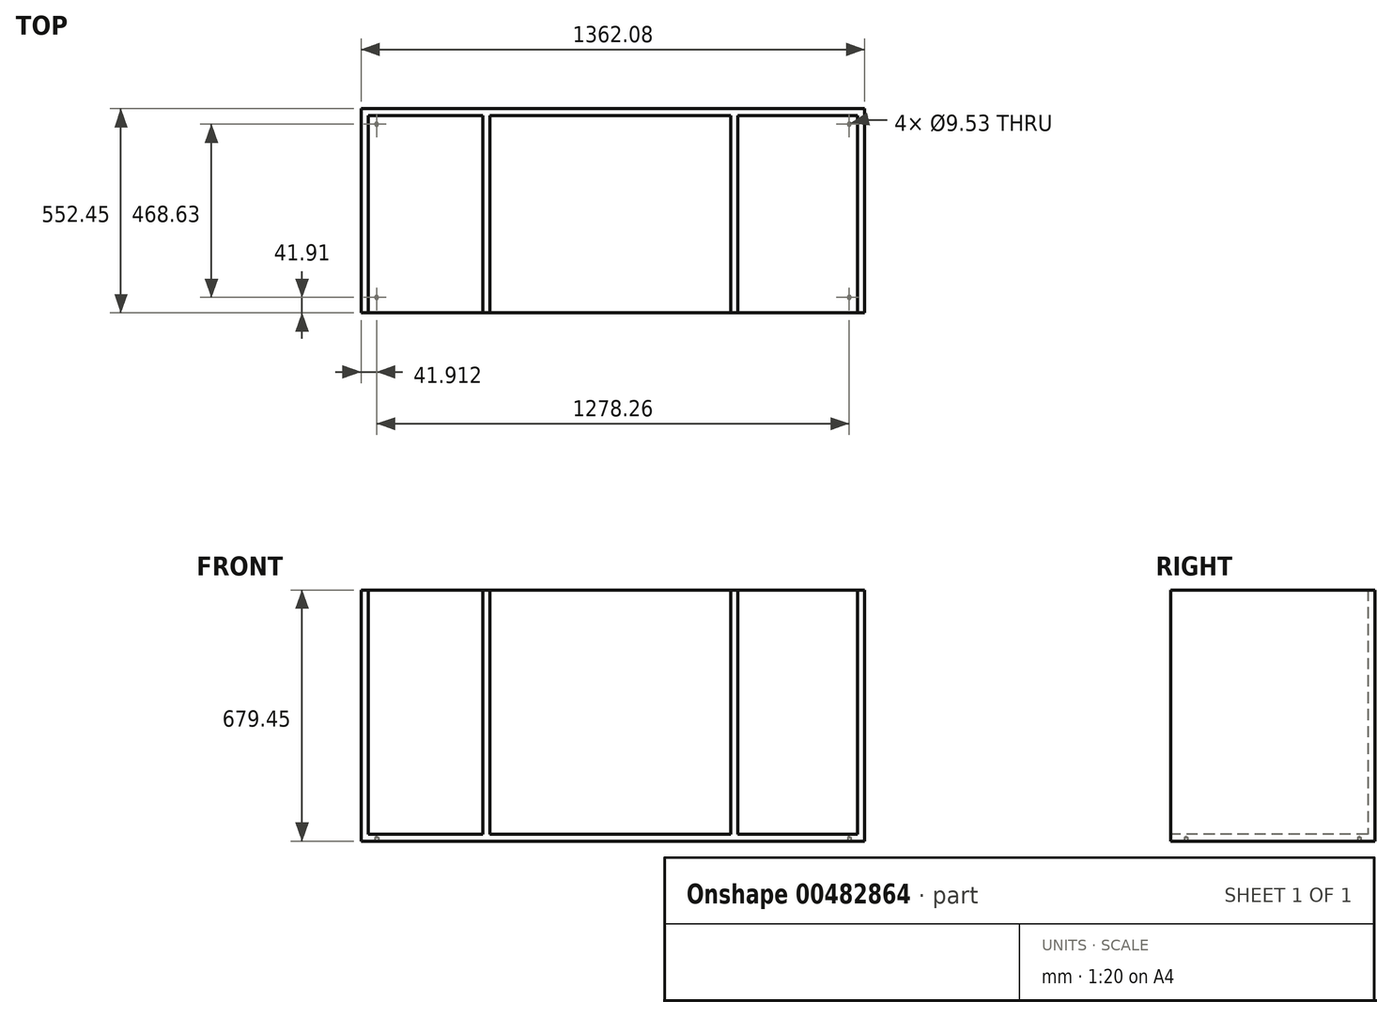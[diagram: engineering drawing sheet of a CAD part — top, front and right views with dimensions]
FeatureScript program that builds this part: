
annotation { "Feature Type Name" : "Feature", "Feature Type Description" : "" }
export const myFeature = defineFeature(function(context is Context, id is Id, definition is map)
    precondition{}
    {
        {
            var Q0;
            Q0=qCreatedBy(makeId("Front.planeOp"),FACE);
            var sketch = newSketch(context, id + "F0", { "sketchPlane" : qUnion([Q0])});
            skLineSegment(sketch, "E0", {"start": v(-681.04, 679.45) * mm, "end": v(-681.04, 0) * mm});
            skLineSegment(sketch, "E1", {"start": v(-681.04, 0) * mm, "end": v(681.04, 0) * mm});
            skLineSegment(sketch, "E2", {"start": v(681.04, 0) * mm, "end": v(681.04, 679.45) * mm});
            skLineSegment(sketch, "E3.0", {"start": v(661.99, 19.05) * mm, "end": v(661.99, 679.45) * mm});
            skLineSegment(sketch, "E3.1", {"start": v(-661.99, 19.05) * mm, "end": v(661.99, 19.05) * mm});
            skLineSegment(sketch, "E3.2", {"start": v(-661.99, 679.45) * mm, "end": v(-661.99, 19.05) * mm});
            skLineSegment(sketch, "E4", {"start": v(-681.04, 679.45) * mm, "end": v(-661.99, 679.45) * mm});
            skLineSegment(sketch, "E5", {"start": v(661.99, 679.45) * mm, "end": v(681.04, 679.45) * mm});
            skSolve(sketch);
        }
        {
            var Q0;
            Q0=makeQuery(id+"F0.imprint","IMPRINT",FACE,{"disambiguationData":[TD([[makeQuery(id+"F0.imprint","IMPRINT",EDGE,{"derivedFrom":sQuery(id+"F0.wireOp",EDGE,"E0")}),1.0]])]});
            extrude(context, id + "F1", {"entities" : qUnion([Q0]), "oppositeDirection" : true, "depth" : 533.4 * mm, "offsetDistance" : 25.4 * mm});
        }
        {
            var Q0;
            Q0=makeQuery(id+"F1.opExtrude","CAP_FACE",FACE,{"disambiguationData":[OSD([sQuery(id+"F0.wireOp",EDGE,"E0"),sQuery(id+"F0.wireOp",EDGE,"E1"),sQuery(id+"F0.wireOp",EDGE,"E2"),sQuery(id+"F0.wireOp",EDGE,"E3.0"),sQuery(id+"F0.wireOp",EDGE,"E3.1"),sQuery(id+"F0.wireOp",EDGE,"E3.2"),sQuery(id+"F0.wireOp",EDGE,"E4"),sQuery(id+"F0.wireOp",EDGE,"E5")])],"isStart":false});
            var sketch = newSketch(context, id + "F2", { "sketchPlane" : qUnion([Q0])});
            skLineSegment(sketch, "E6.0", {"start": v(-681.04, 0) * mm, "end": v(-681.04, 679.45) * mm});
            skLineSegment(sketch, "E7.0", {"start": v(681.04, 0) * mm, "end": v(-681.04, 0) * mm});
            skLineSegment(sketch, "E8.0", {"start": v(681.04, 679.45) * mm, "end": v(681.04, 0) * mm});
            skLineSegment(sketch, "E9", {"start": v(-681.04, 679.45) * mm, "end": v(681.04, 679.45) * mm});
            skSolve(sketch);
        }
        {
            var Q0;
            Q0 = qSketchRegion(id + "F2", true);
            extrude(context, id + "F3", {"entities" : qUnion([Q0]), "operationType" : NewBodyOperationType.ADD, "depth" : 19.05 * mm});
        }
        {
            var Q0;
            Q0=makeQuery(id+"F1.opExtrude","CAP_FACE",FACE,{"disambiguationData":[OSD([sQuery(id+"F0.wireOp",EDGE,"E0"),sQuery(id+"F0.wireOp",EDGE,"E1"),sQuery(id+"F0.wireOp",EDGE,"E2"),sQuery(id+"F0.wireOp",EDGE,"E3.0"),sQuery(id+"F0.wireOp",EDGE,"E3.1"),sQuery(id+"F0.wireOp",EDGE,"E3.2"),sQuery(id+"F0.wireOp",EDGE,"E4"),sQuery(id+"F0.wireOp",EDGE,"E5")])],"isStart":true});
            var sketch = newSketch(context, id + "F4", { "sketchPlane" : qUnion([Q0])});
            skLineSegment(sketch, "E10.bottom", {"start": v(-352.43, 679.45) * mm, "end": v(-333.38, 679.45) * mm});
            skLineSegment(sketch, "E10.top", {"start": v(-352.43, 19.05) * mm, "end": v(-333.38, 19.05) * mm});
            skLineSegment(sketch, "E10.left", {"start": v(-352.43, 679.45) * mm, "end": v(-352.43, 19.05) * mm});
            skLineSegment(sketch, "E10.right", {"start": v(-333.38, 679.45) * mm, "end": v(-333.38, 19.05) * mm});
            skLineSegment(sketch, "E11.bottom", {"start": v(319.09, 679.45) * mm, "end": v(338.14, 679.45) * mm});
            skLineSegment(sketch, "E11.top", {"start": v(319.09, 19.05) * mm, "end": v(338.14, 19.05) * mm});
            skLineSegment(sketch, "E11.left", {"start": v(319.09, 679.45) * mm, "end": v(319.09, 19.05) * mm});
            skLineSegment(sketch, "E11.right", {"start": v(338.14, 679.45) * mm, "end": v(338.14, 19.05) * mm});
            skSolve(sketch);
        }
        {
            var Q0;
            Q0 = qSketchRegion(id + "F4", true);
            var Q1;
            Q1=makeQuery(id+"F3.opExtrude","CAP_FACE",FACE,{"disambiguationData":[OSD([sQuery(id+"F2.wireOp",EDGE,"E6.0"),sQuery(id+"F2.wireOp",EDGE,"E7.0"),sQuery(id+"F2.wireOp",EDGE,"E8.0"),sQuery(id+"F2.wireOp",EDGE,"E9")])],"isStart":true});
            extrude(context, id + "F5", {"entities" : qUnion([Q0]), "operationType" : NewBodyOperationType.ADD, "endBound" : BoundingType.UP_TO_SURFACE, "oppositeDirection" : true, "endBoundEntityFace" : qUnion([Q1]), "depth" : 25.4 * mm});
        }
        {
            var Q0;
            Q0=makeQuery(id+"F3.boolean.opBoolean","MERGE",FACE,{"derivedFrom":[makeQuery(id+"F1.opExtrude","SWEPT_FACE",FACE,{"disambiguationData":[OSD([sQuery(id+"F0.wireOp",EDGE,"E1")])]}),makeQuery(id+"F3.opExtrude","SWEPT_FACE",FACE,{"disambiguationData":[OSD([sQuery(id+"F2.wireOp",EDGE,"E7.0")])]})]});
            var sketch = newSketch(context, id + "F6", { "sketchPlane" : qUnion([Q0])});
            skPoint(sketch, "E12", {"position": v(-639.13, -41.91) * mm});
            skPoint(sketch, "E13", {"position": v(-639.13, -510.54) * mm});
            skPoint(sketch, "E14", {"position": v(639.13, -510.54) * mm});
            skPoint(sketch, "E15", {"position": v(639.13, -41.91) * mm});
            skLineSegment(sketch, "E16.bottom", {"start": v(-639.13, -41.91) * mm, "end": v(639.13, -41.91) * mm, "construction": true});
            skLineSegment(sketch, "E16.top", {"start": v(-639.13, -510.54) * mm, "end": v(639.13, -510.54) * mm, "construction": true});
            skLineSegment(sketch, "E16.left", {"start": v(-639.13, -41.91) * mm, "end": v(-639.13, -510.54) * mm, "construction": true});
            skLineSegment(sketch, "E16.right", {"start": v(639.13, -41.91) * mm, "end": v(639.13, -510.54) * mm, "construction": true});
            skSolve(sketch);
        }
        {
            var Q0;
            Q0=sQuery(id+"F6.wireOp",VERTEX,"E12");
            var Q1;
            Q1=sQuery(id+"F6.wireOp",VERTEX,"E13");
            var Q2;
            Q2=sQuery(id+"F6.wireOp",VERTEX,"E15");
            var Q3;
            Q3=sQuery(id+"F6.wireOp",VERTEX,"E14");
            var Q4;
            Q4=makeQuery(id+"F1.opExtrude","SWEPT_BODY",BODY,{"disambiguationData":[OSD([sQuery(id+"F0.wireOp",EDGE,"E0"),sQuery(id+"F0.wireOp",EDGE,"E1"),sQuery(id+"F0.wireOp",EDGE,"E2"),sQuery(id+"F0.wireOp",EDGE,"E3.0"),sQuery(id+"F0.wireOp",EDGE,"E3.1"),sQuery(id+"F0.wireOp",EDGE,"E3.2"),sQuery(id+"F0.wireOp",EDGE,"E4"),sQuery(id+"F0.wireOp",EDGE,"E5")])]});
            hole(context, id + "F7", {"style" : HoleStyle.SIMPLE, "endStyle" : HoleEndStyle.BLIND, "holeDiameter" : 9.52 * mm, "holeDepth" : 9.52 * mm, "isTappedThrough" : true, "tappedDepth" : 12.7 * mm, "tapClearance" : 3, "startFromSketch" : true, "locations" : qUnion([Q0, Q1, Q2, Q3]), "scope" : qUnion([Q4])});
        }
    });
